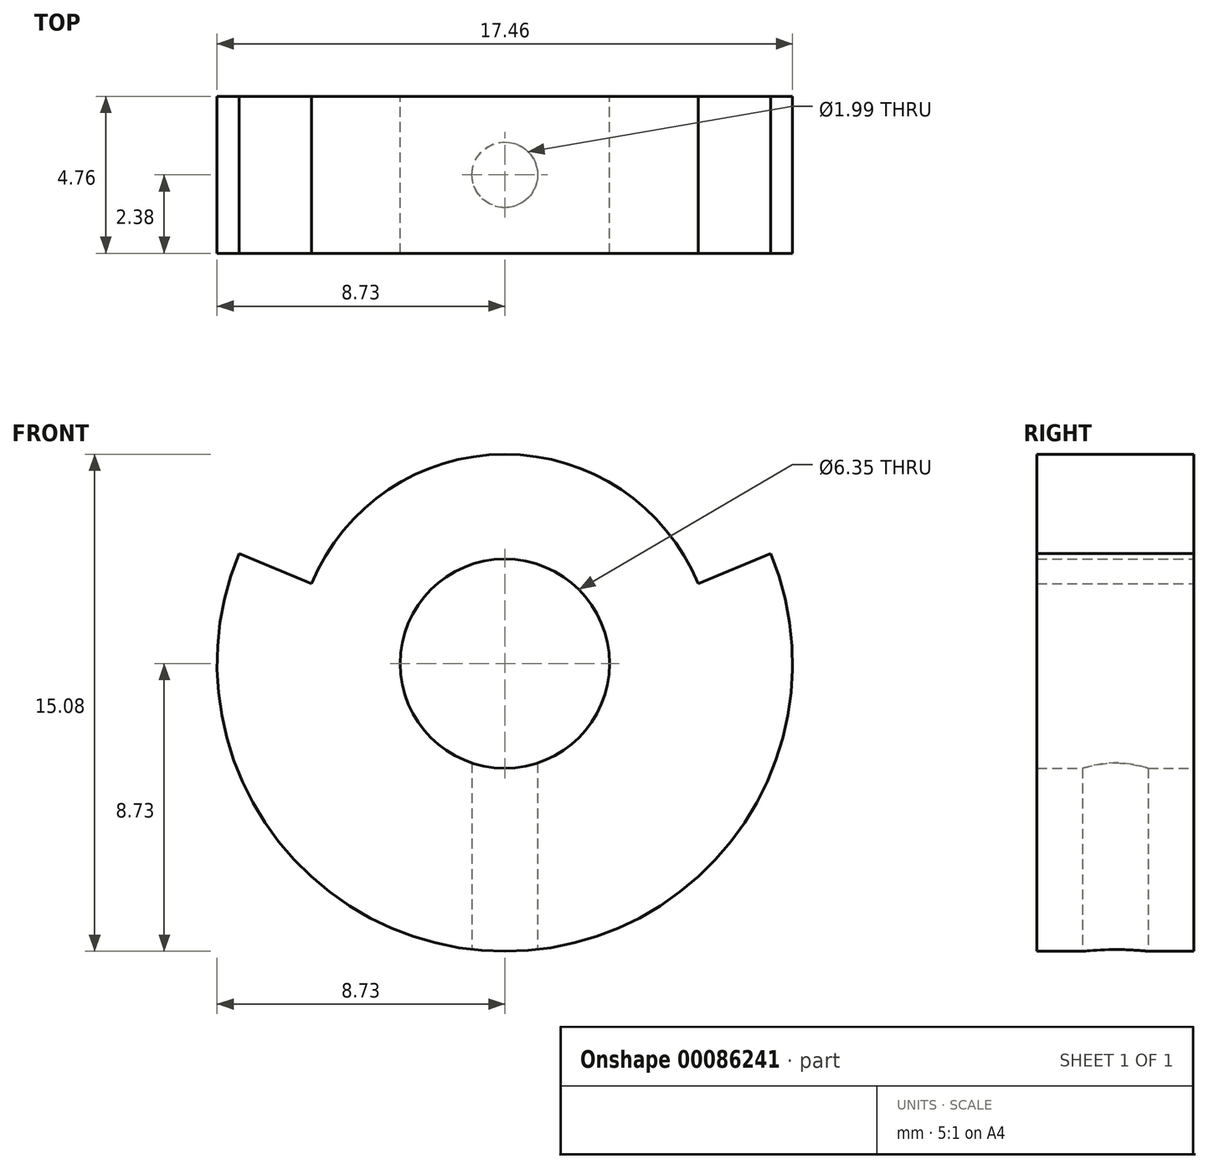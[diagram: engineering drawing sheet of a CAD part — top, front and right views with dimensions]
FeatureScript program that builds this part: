
annotation { "Feature Type Name" : "Feature", "Feature Type Description" : "" }
export const myFeature = defineFeature(function(context is Context, id is Id, definition is map)
    precondition{}
    {
        {
            var Q0;
            Q0=qCreatedBy(makeId("Front.planeOp"),FACE);
            var sketch = newSketch(context, id + "F0", { "sketchPlane" : qUnion([Q0])});
            skArc(sketch, "E0", {"start": v(-8.07, 3.34) * mm, "mid": v(0, -8.73) * mm, "end": v(8.07, 3.34) * mm});
            skLineSegment(sketch, "E1", {"start": v(-8.07, 3.34) * mm, "end": v(-5.87, 2.43) * mm});
            skLineSegment(sketch, "E2", {"start": v(5.87, 2.43) * mm, "end": v(8.07, 3.34) * mm});
            skArc(sketch, "E3", {"start": v(5.87, 2.43) * mm, "mid": v(0, 6.35) * mm, "end": v(-5.87, 2.43) * mm});
            skLineSegment(sketch, "E4", {"start": v(0, 0) * mm, "end": v(0, 10.82) * mm, "construction": true});
            skLineSegment(sketch, "E5", {"start": v(5.87, 2.43) * mm, "end": v(0, 0) * mm, "construction": true});
            skCircle(sketch, "E6", {"center": v(0, 0) * mm, "radius": 3.17 * mm});
            skSolve(sketch);
        }
        {
            var Q0;
            Q0=makeQuery(id+"F0.imprint","IMPRINT",FACE,{"disambiguationData":[TD([[makeQuery(id+"F0.imprint","IMPRINT",EDGE,{"derivedFrom":sQuery(id+"F0.wireOp",EDGE,"E0")}),1.0]])]});
            extrude(context, id + "F1", {"entities" : qUnion([Q0]), "depth" : ((3 / 16) * 25.4) * mm, "symmetric" : true});
        }
        {
            var Q0;
            Q0=qCreatedBy(makeId("Top.planeOp"),FACE);
            var sketch = newSketch(context, id + "F2", { "sketchPlane" : qUnion([Q0])});
            skPoint(sketch, "E7", {"position": v(0, 0) * mm});
            skSolve(sketch);
        }
        {
            var Q0;
            Q0=sQuery(id+"F2.wireOp",VERTEX,"E7");
            var Q1;
            Q1=makeQuery(id+"F1.opExtrude","SWEPT_BODY",BODY,{"disambiguationData":[OSD([sQuery(id+"F0.wireOp",EDGE,"E0"),sQuery(id+"F0.wireOp",EDGE,"E1"),sQuery(id+"F0.wireOp",EDGE,"E2"),sQuery(id+"F0.wireOp",EDGE,"E3"),sQuery(id+"F0.wireOp",EDGE,"E6")])]});
            hole(context, id + "F3", {"style" : HoleStyle.SIMPLE, "endStyle" : HoleEndStyle.THROUGH, "standardTappedOrClearance" : lookupTablePath({ "standard" : "ANSI", "engagement" : "75%", "pitch" : "48 tpi", "size" : "#3", "type" : "Tapped" }), "standardBlindInLast" : lookupTablePath({ "standard" : "ANSI", "engagement" : "75%", "pitch" : "48 tpi", "size" : "#3", "type" : "Tapped" }), "holeDiameter" : 2 * mm, "locations" : qUnion([Q0]), "scope" : qUnion([Q1]), "isTappedThrough" : true, "majorDiameter" : 2.5 * mm, "showTappedDepth" : true});
        }
    });
